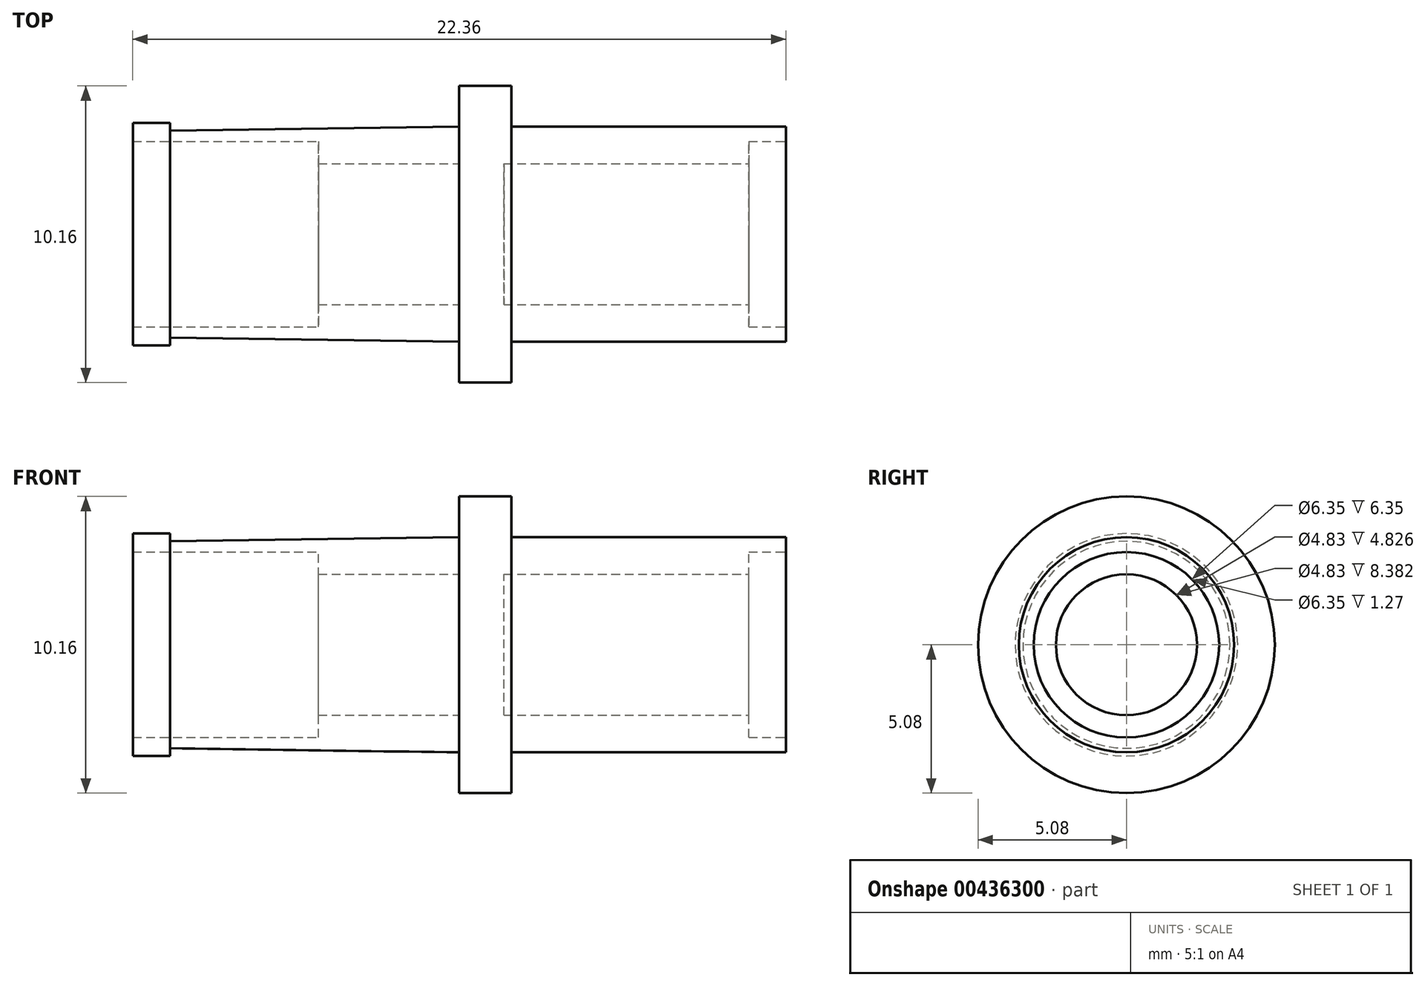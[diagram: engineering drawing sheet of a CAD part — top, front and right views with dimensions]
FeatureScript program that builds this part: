
annotation { "Feature Type Name" : "Feature", "Feature Type Description" : "" }
export const myFeature = defineFeature(function(context is Context, id is Id, definition is map)
    precondition{}
    {
        {
            var Q0;
            Q0=qCreatedBy(makeId("Front.planeOp"),FACE);
            var sketch = newSketch(context, id + "F0", { "sketchPlane" : qUnion([Q0])});
            skLineSegment(sketch, "E0", {"start": v(-14.53, 0) * mm, "end": v(-12.75, 0) * mm});
            skLineSegment(sketch, "E1", {"start": v(-12.75, 0) * mm, "end": v(-12.75, -1.4) * mm});
            skLineSegment(sketch, "E2", {"start": v(-12.75, -1.4) * mm, "end": v(-3.35, -1.4) * mm});
            skLineSegment(sketch, "E3", {"start": v(-3.35, -1.4) * mm, "end": v(-3.35, -1.9) * mm});
            skLineSegment(sketch, "E4", {"start": v(-3.35, -1.9) * mm, "end": v(-4.62, -1.9) * mm});
            skLineSegment(sketch, "E5", {"start": v(-4.62, -1.9) * mm, "end": v(-4.62, -2.67) * mm});
            skLineSegment(sketch, "E6", {"start": v(-14.53, -2.67) * mm, "end": v(-14.53, -5.08) * mm});
            skLineSegment(sketch, "E7", {"start": v(-13, -5.08) * mm, "end": v(-14.53, -5.08) * mm});
            skLineSegment(sketch, "E8", {"start": v(-13, -5.08) * mm, "end": v(-13, -2.67) * mm});
            skLineSegment(sketch, "E9", {"start": v(-19.36, -2.67) * mm, "end": v(-19.36, -1.9) * mm});
            skLineSegment(sketch, "E10", {"start": v(-19.36, -1.9) * mm, "end": v(-25.7, -1.9) * mm});
            skLineSegment(sketch, "E11", {"start": v(-25.7, -1.9) * mm, "end": v(-25.7, -1.27) * mm});
            skLineSegment(sketch, "E12", {"start": v(-25.7, -1.27) * mm, "end": v(-24.44, -1.27) * mm});
            skLineSegment(sketch, "E13", {"start": v(-24.44, -1.27) * mm, "end": v(-24.44, -1.54) * mm});
            skLineSegment(sketch, "E14", {"start": v(-14.53, 0) * mm, "end": v(-14.53, -1.4) * mm});
            skLineSegment(sketch, "E15", {"start": v(-14.53, -1.4) * mm, "end": v(-24.44, -1.54) * mm});
            skLineSegment(sketch, "E16", {"start": v(-19.36, -2.67) * mm, "end": v(-14.53, -2.67) * mm});
            skLineSegment(sketch, "E17", {"start": v(-4.62, -2.67) * mm, "end": v(-13, -2.67) * mm});
            skSolve(sketch);
        }
        {
            var Q0;
            Q0=makeQuery(id+"F0.imprint","IMPRINT",FACE,{"disambiguationData":[TD([[makeQuery(id+"F0.imprint","IMPRINT",EDGE,{"derivedFrom":sQuery(id+"F0.wireOp",EDGE,"E0")}),-1.0]])]});
            var Q1;
            Q1=sQuery(id+"F0.wireOp",EDGE,"E7");
            revolve(context, id + "F1", {"entities" : qUnion([Q0]), "axis" : qUnion([Q1]), "revolveType" : RevolveType.FULL});
        }
    });
